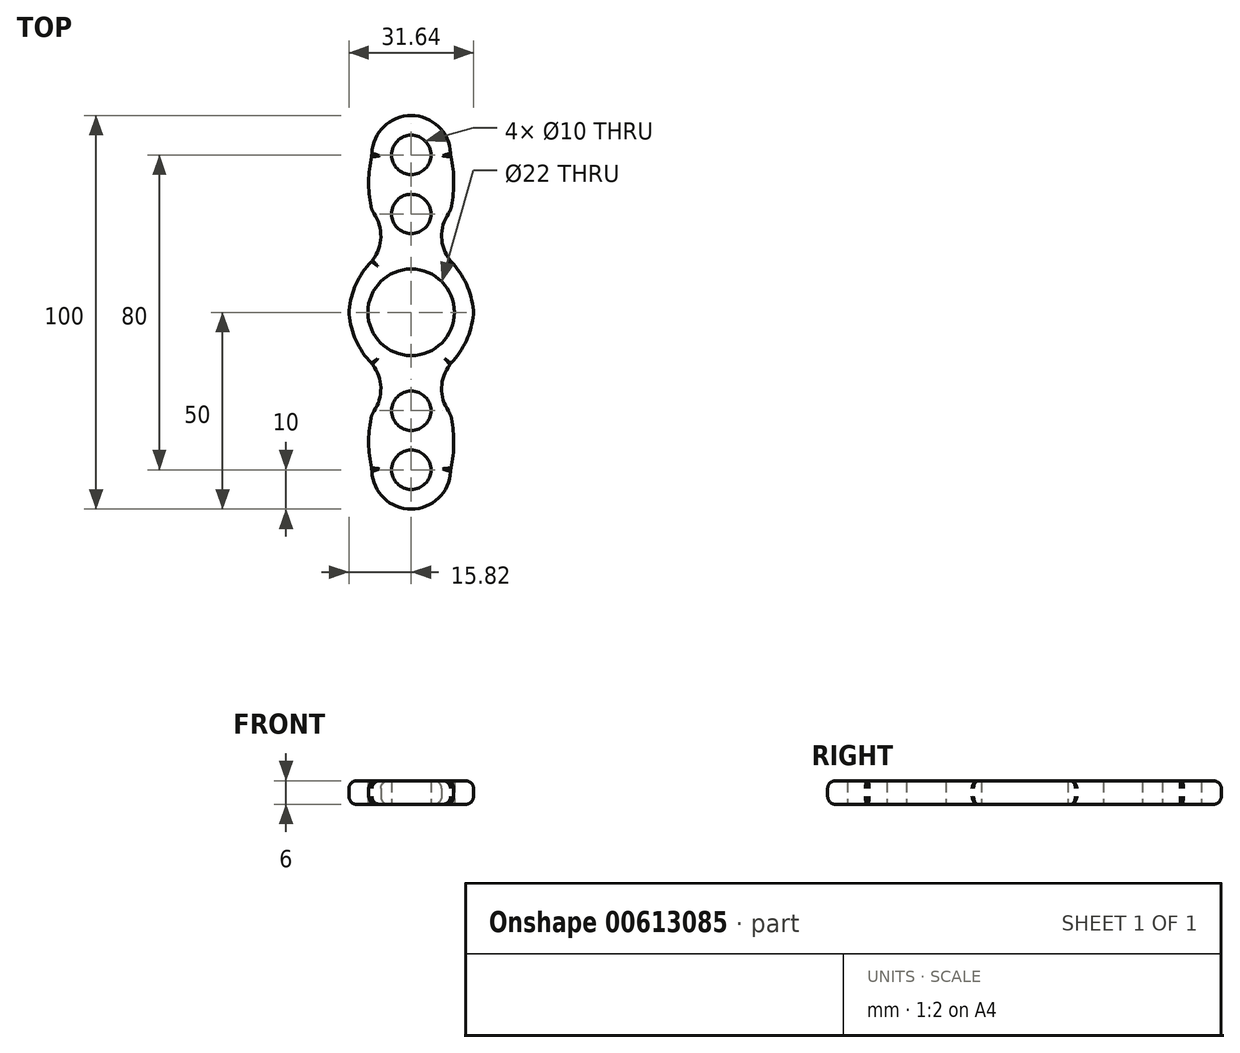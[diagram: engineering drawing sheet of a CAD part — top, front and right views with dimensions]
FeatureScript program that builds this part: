
annotation { "Feature Type Name" : "Feature", "Feature Type Description" : "" }
export const myFeature = defineFeature(function(context is Context, id is Id, definition is map)
    precondition{}
    {
        {
            var Q0;
            Q0=qCreatedBy(makeId("Top.planeOp"),FACE);
            var sketch = newSketch(context, id + "F0", { "sketchPlane" : qUnion([Q0])});
            skCircle(sketch, "E0", {"center": v(0, 0) * mm, "radius": 11 * mm});
            skCircle(sketch, "E1", {"center": v(0, 25) * mm, "radius": 5 * mm});
            skCircle(sketch, "E2", {"center": v(0, 40) * mm, "radius": 5 * mm});
            skCircle(sketch, "E3.1.0", {"center": v(0, -40) * mm, "radius": 5 * mm});
            skCircle(sketch, "E3.1.1", {"center": v(0, -25) * mm, "radius": 5 * mm});
            skArc(sketch, "E4", {"start": v(10, 40) * mm, "mid": v(0, 50) * mm, "end": v(-10, 40) * mm});
            skArc(sketch, "E5", {"start": v(-10, 13.07) * mm, "mid": v(-14.06, 7.04) * mm, "end": v(-15.84, 0) * mm});
            skArc(sketch, "E6.MirrorCS", {"start": v(10, -40) * mm, "mid": v(0, -50) * mm, "end": v(-10, -40) * mm});
            skArc(sketch, "E7", {"start": v(-10, 40) * mm, "mid": v(-10.8, 32.92) * mm, "end": v(-10, 25.84) * mm});
            skArc(sketch, "E8", {"start": v(-10, 13.07) * mm, "mid": v(-7.72, 19.45) * mm, "end": v(-10, 25.84) * mm});
            skArc(sketch, "E9.MirrorCS", {"start": v(10, 40) * mm, "mid": v(10.8, 32.92) * mm, "end": v(10, 25.84) * mm});
            skArc(sketch, "E10.MirrorCS", {"start": v(10, 13.07) * mm, "mid": v(7.72, 19.45) * mm, "end": v(10, 25.84) * mm});
            skArc(sketch, "E11.MirrorCS", {"start": v(10, 13.07) * mm, "mid": v(14.06, 7.04) * mm, "end": v(15.84, 0) * mm});
            skArc(sketch, "E12.MirrorCS", {"start": v(-10, -13.07) * mm, "mid": v(-14.06, -7.04) * mm, "end": v(-15.84, 0) * mm});
            skArc(sketch, "E13.MirrorCS", {"start": v(-10, -13.07) * mm, "mid": v(-7.72, -19.45) * mm, "end": v(-10, -25.84) * mm});
            skArc(sketch, "E14.MirrorCS", {"start": v(-10, -40) * mm, "mid": v(-10.8, -32.92) * mm, "end": v(-10, -25.84) * mm});
            skArc(sketch, "E15.MirrorCS", {"start": v(10, -40) * mm, "mid": v(10.8, -32.92) * mm, "end": v(10, -25.84) * mm});
            skArc(sketch, "E16.MirrorCS", {"start": v(10, -13.07) * mm, "mid": v(7.72, -19.45) * mm, "end": v(10, -25.84) * mm});
            skArc(sketch, "E17.MirrorCS", {"start": v(10, -13.07) * mm, "mid": v(14.06, -7.04) * mm, "end": v(15.84, 0) * mm});
            skSolve(sketch);
        }
        {
            var Q0;
            Q0=makeQuery(id+"F0.imprint","IMPRINT",FACE,{"disambiguationData":[TD([[makeQuery(id+"F0.imprint","IMPRINT",EDGE,{"derivedFrom":sQuery(id+"F0.wireOp",EDGE,"E0")}),-1.0]])]});
            extrude(context, id + "F1", {"entities" : qUnion([Q0]), "depth" : 6 * mm, "offsetDistance" : 25 * mm});
        }
        {
            var Q0;
            Q0=makeQuery(id+"F1.opExtrude","CAP_EDGE",EDGE,{"disambiguationData":[OSD([sQuery(id+"F0.wireOp",EDGE,"E8")])],"isStart":false});
            var Q1;
            Q1=makeQuery(id+"F1.opExtrude","CAP_EDGE",EDGE,{"disambiguationData":[OSD([sQuery(id+"F0.wireOp",EDGE,"E7")])],"isStart":false});
            var Q2;
            Q2=makeQuery(id+"F1.opExtrude","CAP_EDGE",EDGE,{"disambiguationData":[OSD([sQuery(id+"F0.wireOp",EDGE,"E4")])],"isStart":false});
            var Q3;
            Q3=makeQuery(id+"F1.opExtrude","CAP_EDGE",EDGE,{"disambiguationData":[OSD([sQuery(id+"F0.wireOp",EDGE,"E9.MirrorCS")])],"isStart":false});
            var Q4;
            Q4=makeQuery(id+"F1.opExtrude","CAP_EDGE",EDGE,{"disambiguationData":[OSD([sQuery(id+"F0.wireOp",EDGE,"E10.MirrorCS")])],"isStart":false});
            var Q5;
            Q5=makeQuery(id+"F1.opExtrude","CAP_EDGE",EDGE,{"disambiguationData":[OSD([sQuery(id+"F0.wireOp",EDGE,"E17.MirrorCS")])],"isStart":false});
            var Q6;
            Q6=makeQuery(id+"F1.opExtrude","CAP_EDGE",EDGE,{"disambiguationData":[OSD([sQuery(id+"F0.wireOp",EDGE,"E11.MirrorCS")])],"isStart":false});
            var Q7;
            Q7=makeQuery(id+"F1.opExtrude","CAP_EDGE",EDGE,{"disambiguationData":[OSD([sQuery(id+"F0.wireOp",EDGE,"E16.MirrorCS")])],"isStart":false});
            var Q8;
            Q8=makeQuery(id+"F1.opExtrude","CAP_EDGE",EDGE,{"disambiguationData":[OSD([sQuery(id+"F0.wireOp",EDGE,"E15.MirrorCS")])],"isStart":false});
            var Q9;
            Q9=makeQuery(id+"F1.opExtrude","CAP_EDGE",EDGE,{"disambiguationData":[OSD([sQuery(id+"F0.wireOp",EDGE,"E6.MirrorCS")])],"isStart":false});
            var Q10;
            Q10=makeQuery(id+"F1.opExtrude","CAP_EDGE",EDGE,{"disambiguationData":[OSD([sQuery(id+"F0.wireOp",EDGE,"E14.MirrorCS")])],"isStart":false});
            var Q11;
            Q11=makeQuery(id+"F1.opExtrude","CAP_EDGE",EDGE,{"disambiguationData":[OSD([sQuery(id+"F0.wireOp",EDGE,"E13.MirrorCS")])],"isStart":false});
            var Q12;
            Q12=makeQuery(id+"F1.opExtrude","CAP_EDGE",EDGE,{"disambiguationData":[OSD([sQuery(id+"F0.wireOp",EDGE,"E12.MirrorCS")])],"isStart":false});
            var Q13;
            Q13=makeQuery(id+"F1.opExtrude","CAP_EDGE",EDGE,{"disambiguationData":[OSD([sQuery(id+"F0.wireOp",EDGE,"E5")])],"isStart":false});
            var Q14;
            Q14=makeQuery(id+"F1.opExtrude","CAP_EDGE",EDGE,{"disambiguationData":[OSD([sQuery(id+"F0.wireOp",EDGE,"E6.MirrorCS")])],"isStart":true});
            var Q15;
            Q15=makeQuery(id+"F1.opExtrude","CAP_EDGE",EDGE,{"disambiguationData":[OSD([sQuery(id+"F0.wireOp",EDGE,"E15.MirrorCS")])],"isStart":true});
            var Q16;
            Q16=makeQuery(id+"F1.opExtrude","CAP_EDGE",EDGE,{"disambiguationData":[OSD([sQuery(id+"F0.wireOp",EDGE,"E14.MirrorCS")])],"isStart":true});
            var Q17;
            Q17=makeQuery(id+"F1.opExtrude","CAP_EDGE",EDGE,{"disambiguationData":[OSD([sQuery(id+"F0.wireOp",EDGE,"E13.MirrorCS")])],"isStart":true});
            var Q18;
            Q18=makeQuery(id+"F1.opExtrude","CAP_EDGE",EDGE,{"disambiguationData":[OSD([sQuery(id+"F0.wireOp",EDGE,"E12.MirrorCS")])],"isStart":true});
            var Q19;
            Q19=makeQuery(id+"F1.opExtrude","CAP_EDGE",EDGE,{"disambiguationData":[OSD([sQuery(id+"F0.wireOp",EDGE,"E5")])],"isStart":true});
            var Q20;
            Q20=makeQuery(id+"F1.opExtrude","CAP_EDGE",EDGE,{"disambiguationData":[OSD([sQuery(id+"F0.wireOp",EDGE,"E8")])],"isStart":true});
            var Q21;
            Q21=makeQuery(id+"F1.opExtrude","CAP_EDGE",EDGE,{"disambiguationData":[OSD([sQuery(id+"F0.wireOp",EDGE,"E7")])],"isStart":true});
            var Q22;
            Q22=makeQuery(id+"F1.opExtrude","CAP_EDGE",EDGE,{"disambiguationData":[OSD([sQuery(id+"F0.wireOp",EDGE,"E4")])],"isStart":true});
            var Q23;
            Q23=makeQuery(id+"F1.opExtrude","CAP_EDGE",EDGE,{"disambiguationData":[OSD([sQuery(id+"F0.wireOp",EDGE,"E9.MirrorCS")])],"isStart":true});
            var Q24;
            Q24=makeQuery(id+"F1.opExtrude","CAP_EDGE",EDGE,{"disambiguationData":[OSD([sQuery(id+"F0.wireOp",EDGE,"E10.MirrorCS")])],"isStart":true});
            var Q25;
            Q25=makeQuery(id+"F1.opExtrude","CAP_EDGE",EDGE,{"disambiguationData":[OSD([sQuery(id+"F0.wireOp",EDGE,"E11.MirrorCS")])],"isStart":true});
            var Q26;
            Q26=makeQuery(id+"F1.opExtrude","CAP_EDGE",EDGE,{"disambiguationData":[OSD([sQuery(id+"F0.wireOp",EDGE,"E17.MirrorCS")])],"isStart":true});
            var Q27;
            Q27=makeQuery(id+"F1.opExtrude","CAP_EDGE",EDGE,{"disambiguationData":[OSD([sQuery(id+"F0.wireOp",EDGE,"E16.MirrorCS")])],"isStart":true});
            fillet(context, id + "F2", {"entities" : qUnion([Q0, Q1, Q2, Q3, Q4, Q5, Q6, Q7, Q8, Q9, Q10, Q11, Q12, Q13, Q14, Q15, Q16, Q17, Q18, Q19, Q20, Q21, Q22, Q23, Q24, Q25, Q26, Q27]), "radius" : 2 * mm, "tangentPropagation" : true, "allowEdgeOverflow" : false});
        }
        {
            var Q0;
            Q0=makeQuery(id+"F1.opExtrude","SWEPT_EDGE",EDGE,{"disambiguationData":[OSD([sQuery(id+"F0.wireOp",EDGE,"E9.MirrorCS"),sQuery(id+"F0.wireOp",EDGE,"E10.MirrorCS")])]});
            var Q1;
            Q1=makeQuery(id+"F1.opExtrude","SWEPT_EDGE",EDGE,{"disambiguationData":[OSD([sQuery(id+"F0.wireOp",EDGE,"E4"),sQuery(id+"F0.wireOp",EDGE,"E9.MirrorCS")])]});
            var Q2;
            Q2=makeQuery(id+"F1.opExtrude","SWEPT_EDGE",EDGE,{"disambiguationData":[OSD([sQuery(id+"F0.wireOp",EDGE,"E10.MirrorCS"),sQuery(id+"F0.wireOp",EDGE,"E11.MirrorCS")])]});
            var Q3;
            Q3=makeQuery(id+"F1.opExtrude","SWEPT_EDGE",EDGE,{"disambiguationData":[OSD([sQuery(id+"F0.wireOp",EDGE,"E11.MirrorCS"),sQuery(id+"F0.wireOp",EDGE,"E17.MirrorCS")])]});
            var Q4;
            Q4=makeQuery(id+"F1.opExtrude","SWEPT_EDGE",EDGE,{"disambiguationData":[OSD([sQuery(id+"F0.wireOp",EDGE,"E16.MirrorCS"),sQuery(id+"F0.wireOp",EDGE,"E17.MirrorCS")])]});
            var Q5;
            Q5=makeQuery(id+"F1.opExtrude","SWEPT_EDGE",EDGE,{"disambiguationData":[OSD([sQuery(id+"F0.wireOp",EDGE,"E15.MirrorCS"),sQuery(id+"F0.wireOp",EDGE,"E16.MirrorCS")])]});
            var Q6;
            Q6=makeQuery(id+"F1.opExtrude","SWEPT_EDGE",EDGE,{"disambiguationData":[OSD([sQuery(id+"F0.wireOp",EDGE,"E6.MirrorCS"),sQuery(id+"F0.wireOp",EDGE,"E15.MirrorCS")])]});
            var Q7;
            Q7=makeQuery(id+"F1.opExtrude","SWEPT_EDGE",EDGE,{"disambiguationData":[OSD([sQuery(id+"F0.wireOp",EDGE,"E6.MirrorCS"),sQuery(id+"F0.wireOp",EDGE,"E14.MirrorCS")])]});
            var Q8;
            Q8=makeQuery(id+"F1.opExtrude","SWEPT_EDGE",EDGE,{"disambiguationData":[OSD([sQuery(id+"F0.wireOp",EDGE,"E13.MirrorCS"),sQuery(id+"F0.wireOp",EDGE,"E14.MirrorCS")])]});
            var Q9;
            Q9=makeQuery(id+"F1.opExtrude","SWEPT_EDGE",EDGE,{"disambiguationData":[OSD([sQuery(id+"F0.wireOp",EDGE,"E12.MirrorCS"),sQuery(id+"F0.wireOp",EDGE,"E13.MirrorCS")])]});
            var Q10;
            Q10=makeQuery(id+"F1.opExtrude","SWEPT_EDGE",EDGE,{"disambiguationData":[OSD([sQuery(id+"F0.wireOp",EDGE,"E5"),sQuery(id+"F0.wireOp",EDGE,"E12.MirrorCS")])]});
            var Q11;
            Q11=makeQuery(id+"F1.opExtrude","SWEPT_EDGE",EDGE,{"disambiguationData":[OSD([sQuery(id+"F0.wireOp",EDGE,"E5"),sQuery(id+"F0.wireOp",EDGE,"E8")])]});
            var Q12;
            Q12=makeQuery(id+"F1.opExtrude","SWEPT_EDGE",EDGE,{"disambiguationData":[OSD([sQuery(id+"F0.wireOp",EDGE,"E7"),sQuery(id+"F0.wireOp",EDGE,"E8")])]});
            var Q13;
            Q13=makeQuery(id+"F1.opExtrude","SWEPT_EDGE",EDGE,{"disambiguationData":[OSD([sQuery(id+"F0.wireOp",EDGE,"E4"),sQuery(id+"F0.wireOp",EDGE,"E7")])]});
            fillet(context, id + "F3", {"entities" : qUnion([Q0, Q1, Q2, Q3, Q4, Q5, Q6, Q7, Q8, Q9, Q10, Q11, Q12, Q13]), "radius" : 5 * mm, "tangentPropagation" : true, "allowEdgeOverflow" : false});
        }
    });
